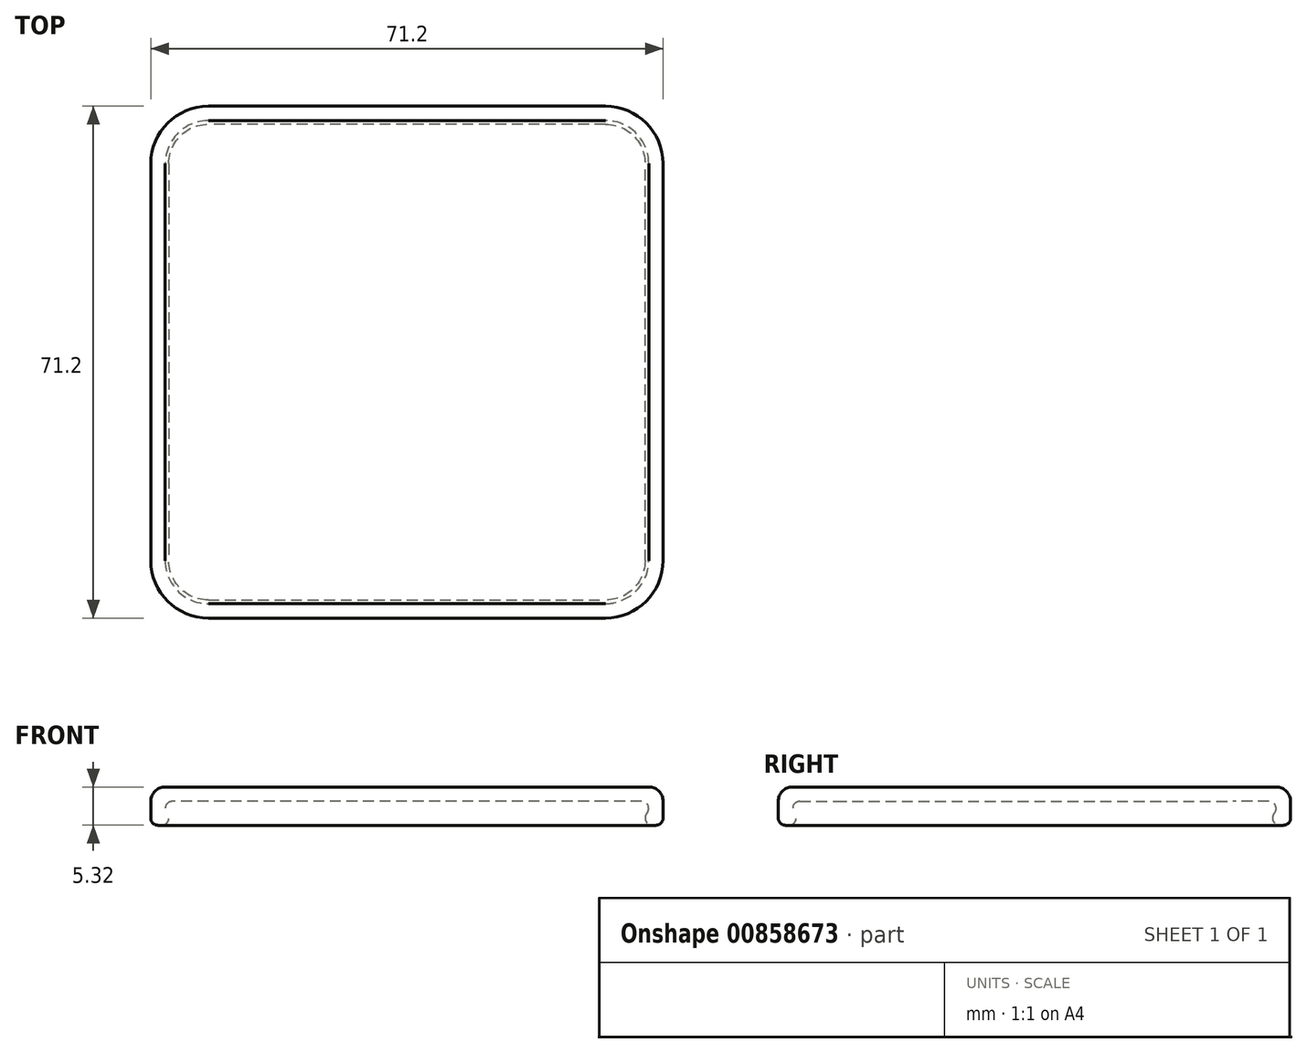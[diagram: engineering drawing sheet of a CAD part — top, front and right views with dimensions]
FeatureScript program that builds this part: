
annotation { "Feature Type Name" : "Feature", "Feature Type Description" : "" }
export const myFeature = defineFeature(function(context is Context, id is Id, definition is map)
    precondition{}
    {
        {
            var Q0;
            Q0=qCreatedBy(makeId("Top.planeOp"),FACE);
            var sketch = newSketch(context, id + "F0", { "sketchPlane" : qUnion([Q0])});
            skPoint(sketch, "E0.0", {"position": v(0, 0) * mm});
            skLineSegment(sketch, "E1.bottom", {"start": v(27.6, -32.6) * mm, "end": v(-27.6, -32.6) * mm});
            skLineSegment(sketch, "E1.top", {"start": v(27.6, 32.6) * mm, "end": v(-27.6, 32.6) * mm});
            skLineSegment(sketch, "E1.left", {"start": v(32.6, -27.6) * mm, "end": v(32.6, 27.6) * mm});
            skLineSegment(sketch, "E1.right", {"start": v(-32.6, -27.6) * mm, "end": v(-32.6, 27.6) * mm});
            skPoint(sketch, "E2.visualSharp", {"position": v(-32.6, 32.6) * mm});
            skArc(sketch, "E2.filletArc", {"start": v(-27.6, 32.6) * mm, "mid": v(-31.14, 31.14) * mm, "end": v(-32.6, 27.6) * mm});
            skPoint(sketch, "E3.visualSharp", {"position": v(32.6, 32.6) * mm});
            skArc(sketch, "E3.filletArc", {"start": v(32.6, 27.6) * mm, "mid": v(31.14, 31.14) * mm, "end": v(27.6, 32.6) * mm});
            skPoint(sketch, "E4.visualSharp", {"position": v(32.6, -32.6) * mm});
            skArc(sketch, "E4.filletArc", {"start": v(27.6, -32.6) * mm, "mid": v(31.14, -31.14) * mm, "end": v(32.6, -27.6) * mm});
            skPoint(sketch, "E5.visualSharp", {"position": v(-32.6, -32.6) * mm});
            skArc(sketch, "E5.filletArc", {"start": v(-32.6, -27.6) * mm, "mid": v(-31.14, -31.14) * mm, "end": v(-27.6, -32.6) * mm});
            skSolve(sketch);
        }
        {
            var Q0;
            Q0=qCreatedBy(makeId("Front.planeOp"),FACE);
            var sketch = newSketch(context, id + "F1", { "sketchPlane" : qUnion([Q0])});
            skArc(sketch, "E6", {"start": v(-32.6, 0) * mm, "mid": v(-33.51, -0.59) * mm, "end": v(-33.35, -1.66) * mm});
            skLineSegment(sketch, "E7", {"start": v(-34.1, -3.32) * mm, "end": v(-34.6, -3.32) * mm});
            skLineSegment(sketch, "E8", {"start": v(-35.6, -2.32) * mm, "end": v(-35.6, 0) * mm});
            skLineSegment(sketch, "E9", {"start": v(-35.6, 0) * mm, "end": v(-32.6, 0) * mm});
            skPoint(sketch, "E10.visualSharp", {"position": v(-32.6, -2) * mm});
            skArc(sketch, "E10.filletArc", {"start": v(-34.1, -3.32) * mm, "mid": v(-33.19, -2.73) * mm, "end": v(-33.35, -1.66) * mm});
            skArc(sketch, "E11.filletArc", {"start": v(-35.6, -2.32) * mm, "mid": v(-35.3, -3.03) * mm, "end": v(-34.6, -3.32) * mm});
            skLineSegment(sketch, "E12", {"start": v(-32.6, 0) * mm, "end": v(-32.6, -3.53) * mm, "construction": true});
            skSolve(sketch);
        }
        {
            var Q0;
            Q0=makeQuery(id+"F1.imprint","IMPRINT",FACE,{"disambiguationData":[TD([[makeQuery(id+"F1.imprint","IMPRINT",EDGE,{"derivedFrom":sQuery(id+"F1.wireOp",EDGE,"E6")}),-1.0]])]});
            var Q1;
            Q1=sQuery(id+"F0.wireOp",EDGE,"E1.right");
            var Q2;
            Q2=sQuery(id+"F0.wireOp",EDGE,"E2.filletArc");
            var Q3;
            Q3=sQuery(id+"F0.wireOp",EDGE,"E1.top");
            var Q4;
            Q4=sQuery(id+"F0.wireOp",EDGE,"E3.filletArc");
            var Q5;
            Q5=sQuery(id+"F0.wireOp",EDGE,"E1.left");
            var Q6;
            Q6=sQuery(id+"F0.wireOp",EDGE,"E4.filletArc");
            var Q7;
            Q7=sQuery(id+"F0.wireOp",EDGE,"E1.bottom");
            var Q8;
            Q8=sQuery(id+"F0.wireOp",EDGE,"E5.filletArc");
            sweep(context, id + "F2", {"profiles" : qUnion([Q0]), "path" : qUnion([Q1, Q2, Q3, Q4, Q5, Q6, Q7, Q8])});
        }
        {
            var Q0;
            Q0=makeQuery(id+"F2.opSweep","SWEPT_FACE",FACE,{"disambiguationData":[OSD([sQuery(id+"F0.wireOp",EDGE,"E1.right"),sQuery(id+"F1.wireOp",EDGE,"E9")])]});
            var sketch = newSketch(context, id + "F3", { "sketchPlane" : qUnion([Q0])});
            skLineSegment(sketch, "E13.0", {"start": v(-35.6, 27.6) * mm, "end": v(-35.6, -27.6) * mm});
            skArc(sketch, "E14.0", {"start": v(-27.6, 35.6) * mm, "mid": v(-33.26, 33.26) * mm, "end": v(-35.6, 27.6) * mm});
            skLineSegment(sketch, "E15.0", {"start": v(27.6, 35.6) * mm, "end": v(-27.6, 35.6) * mm});
            skArc(sketch, "E16.0", {"start": v(35.6, 27.6) * mm, "mid": v(33.26, 33.26) * mm, "end": v(27.6, 35.6) * mm});
            skLineSegment(sketch, "E17.0", {"start": v(35.6, -27.6) * mm, "end": v(35.6, 27.6) * mm});
            skArc(sketch, "E18.0", {"start": v(27.6, -35.6) * mm, "mid": v(33.26, -33.26) * mm, "end": v(35.6, -27.6) * mm});
            skLineSegment(sketch, "E19.0", {"start": v(-27.6, -35.6) * mm, "end": v(27.6, -35.6) * mm});
            skArc(sketch, "E20.0", {"start": v(-35.6, -27.6) * mm, "mid": v(-33.26, -33.26) * mm, "end": v(-27.6, -35.6) * mm});
            skSolve(sketch);
        }
        {
            var Q0;
            Q0 = qSketchRegion(id + "F3", true);
            extrude(context, id + "F4", {"entities" : qUnion([Q0]), "operationType" : NewBodyOperationType.ADD, "depth" : 2 * mm, "offsetDistance" : 25 * mm});
        }
        {
            var Q0;
            Q0=makeQuery(id+"F4.opExtrude","CAP_FACE",FACE,{"disambiguationData":[OSD([sQuery(id+"F3.wireOp",EDGE,"E13.0"),sQuery(id+"F3.wireOp",EDGE,"E14.0"),sQuery(id+"F3.wireOp",EDGE,"E15.0"),sQuery(id+"F3.wireOp",EDGE,"E16.0"),sQuery(id+"F3.wireOp",EDGE,"E17.0"),sQuery(id+"F3.wireOp",EDGE,"E18.0"),sQuery(id+"F3.wireOp",EDGE,"E19.0"),sQuery(id+"F3.wireOp",EDGE,"E20.0")])],"isStart":false});
            fillet(context, id + "F5", {"entities" : qUnion([Q0]), "radius" : 2 * mm, "tangentPropagation" : true, "allowEdgeOverflow" : false});
        }
    });
